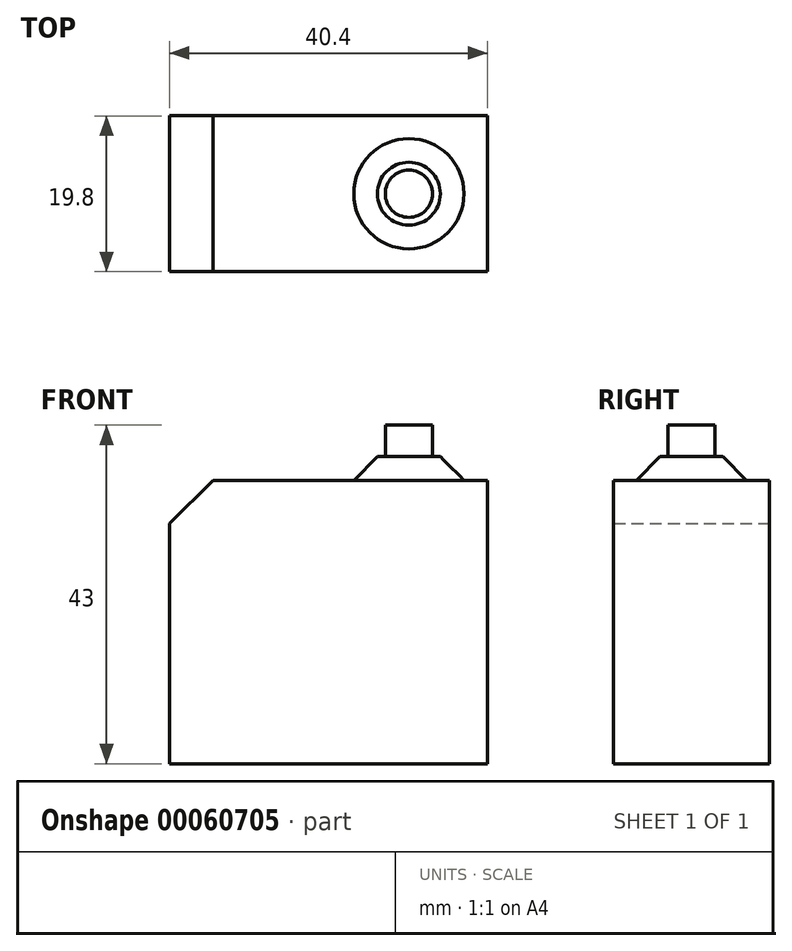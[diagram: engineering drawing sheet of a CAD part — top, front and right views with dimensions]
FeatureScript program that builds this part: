
annotation { "Feature Type Name" : "Feature", "Feature Type Description" : "" }
export const myFeature = defineFeature(function(context is Context, id is Id, definition is map)
    precondition{}
    {
        {
            var Q0;
            Q0=qCreatedBy(makeId("Top.planeOp"),FACE);
            var sketch = newSketch(context, id + "F0", { "sketchPlane" : qUnion([Q0])});
            skLineSegment(sketch, "E0.bottom", {"start": v(-19.55, 6.3) * mm, "end": v(20.85, 6.3) * mm});
            skLineSegment(sketch, "E0.top", {"start": v(-19.55, -13.5) * mm, "end": v(20.85, -13.5) * mm});
            skLineSegment(sketch, "E0.left", {"start": v(-19.55, 6.3) * mm, "end": v(-19.55, -13.5) * mm});
            skLineSegment(sketch, "E0.right", {"start": v(20.85, 6.3) * mm, "end": v(20.85, -13.5) * mm});
            skSolve(sketch);
        }
        {
            var Q0;
            Q0=makeQuery(id+"F0.imprint","IMPRINT",FACE,{"disambiguationData":[TD([[makeQuery(id+"F0.imprint","IMPRINT",EDGE,{"derivedFrom":sQuery(id+"F0.wireOp",EDGE,"E0.bottom")}),-1.0]])]});
            extrude(context, id + "F1", {"entities" : qUnion([Q0]), "depth" : 36 * mm});
        }
        {
            var Q0;
            Q0=makeQuery(id+"F1.opExtrude","CAP_EDGE",EDGE,{"disambiguationData":[OSD([sQuery(id+"F0.wireOp",EDGE,"E0.left")])],"isStart":false});
            chamfer(context, id + "F2", {"entities" : qUnion([Q0]), "width" : 5.5 * mm, "tangentPropagation" : true});
        }
        {
            var Q0;
            Q0=makeQuery(id+"F1.opExtrude","CAP_FACE",FACE,{"disambiguationData":[OSD([sQuery(id+"F0.wireOp",EDGE,"E0.bottom"),sQuery(id+"F0.wireOp",EDGE,"E0.top"),sQuery(id+"F0.wireOp",EDGE,"E0.left"),sQuery(id+"F0.wireOp",EDGE,"E0.right")])],"isStart":false});
            var sketch = newSketch(context, id + "F3", { "sketchPlane" : qUnion([Q0])});
            skCircle(sketch, "E1", {"center": v(10.85, -3.6) * mm, "radius": 7 * mm});
            skCircle(sketch, "E2", {"center": v(10.85, -3.6) * mm, "radius": 5 * mm});
            skSolve(sketch);
        }
        {
            var Q0;
            Q0=makeQuery(id+"F3.imprint","IMPRINT",FACE,{"disambiguationData":[TD([[makeQuery(id+"F3.imprint","IMPRINT",EDGE,{"derivedFrom":sQuery(id+"F3.wireOp",EDGE,"E1")}),1.0]])]});
            extrude(context, id + "F4", {"entities" : qUnion([Q0]), "operationType" : NewBodyOperationType.ADD, "depth" : 3 * mm});
        }
        {
            var Q0;
            Q0=makeQuery(id+"F4.boolean.opBoolean","SPLIT",FACE,{"disambiguationData":[TD([makeQuery(id+"F4.opExtrude","SWEPT_FACE",FACE,{"disambiguationData":[OSD([sQuery(id+"F3.wireOp",EDGE,"E2")])]})])],"derivedFrom":makeQuery(id+"F1.opExtrude","CAP_FACE",FACE,{"disambiguationData":[OSD([sQuery(id+"F0.wireOp",EDGE,"E0.bottom"),sQuery(id+"F0.wireOp",EDGE,"E0.top"),sQuery(id+"F0.wireOp",EDGE,"E0.left"),sQuery(id+"F0.wireOp",EDGE,"E0.right")])],"isStart":false})});
            extrude(context, id + "F5", {"entities" : qUnion([Q0]), "operationType" : NewBodyOperationType.ADD, "depth" : 3 * mm});
        }
        {
            var Q0;
            Q0=makeQuery(id+"F4.opExtrude","CAP_EDGE",EDGE,{"disambiguationData":[OSD([sQuery(id+"F3.wireOp",EDGE,"E1")])],"isStart":false});
            chamfer(context, id + "F6", {"entities" : qUnion([Q0]), "width" : 3 * mm, "tangentPropagation" : true});
        }
        {
            var Q0;
            Q0=makeQuery(id+"F5.boolean.opBoolean","MERGE",FACE,{"derivedFrom":[makeQuery(id+"F4.opExtrude","CAP_FACE",FACE,{"disambiguationData":[OSD([sQuery(id+"F3.wireOp",EDGE,"E1"),sQuery(id+"F3.wireOp",EDGE,"E2")])],"isStart":false}),makeQuery(id+"F5.opExtrude","CAP_FACE",FACE,{"disambiguationData":[OSD([sQuery(id+"F0.wireOp",EDGE,"E0.bottom"),sQuery(id+"F0.wireOp",EDGE,"E0.top"),sQuery(id+"F0.wireOp",EDGE,"E0.left"),sQuery(id+"F0.wireOp",EDGE,"E0.right")])],"isStart":false})]});
            var sketch = newSketch(context, id + "F7", { "sketchPlane" : qUnion([Q0])});
            skCircle(sketch, "E3", {"center": v(10.85, -3.6) * mm, "radius": 3 * mm});
            skSolve(sketch);
        }
        {
            var Q0;
            Q0=makeQuery(id+"F7.imprint","IMPRINT",FACE,{"disambiguationData":[TD([[makeQuery(id+"F7.imprint","IMPRINT",EDGE,{"derivedFrom":sQuery(id+"F7.wireOp",EDGE,"E3")}),1.0]])]});
            extrude(context, id + "F8", {"entities" : qUnion([Q0]), "operationType" : NewBodyOperationType.ADD, "depth" : 4 * mm});
        }
    });
